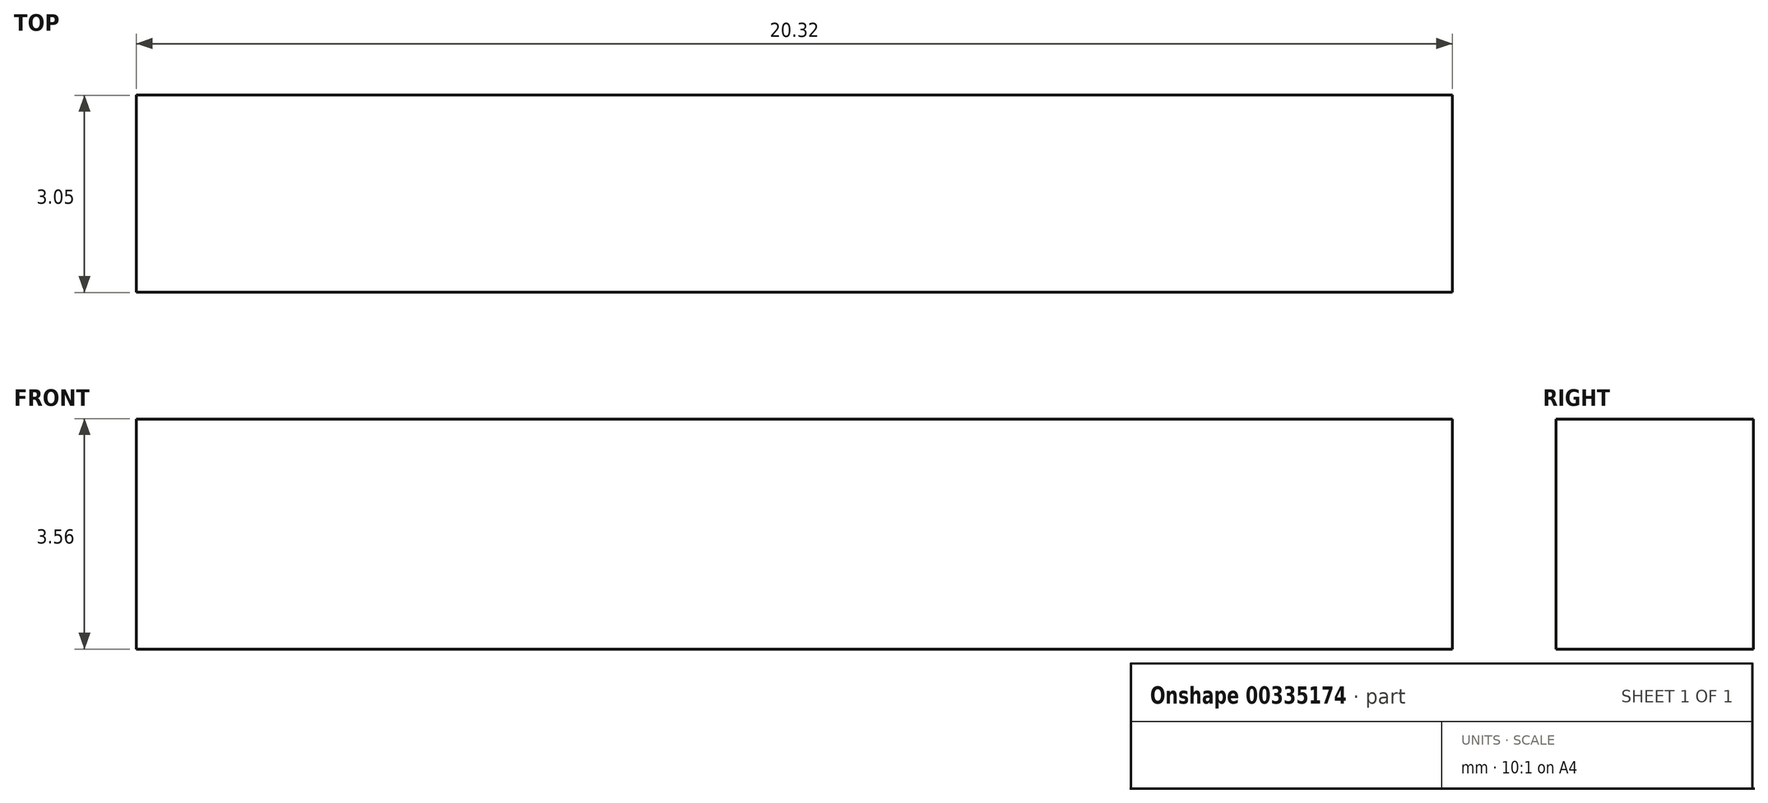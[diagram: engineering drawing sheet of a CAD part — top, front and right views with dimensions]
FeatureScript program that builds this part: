
annotation { "Feature Type Name" : "Feature", "Feature Type Description" : "" }
export const myFeature = defineFeature(function(context is Context, id is Id, definition is map)
    precondition{}
    {
        {
            var Q0;
            Q0=qCreatedBy(makeId("Top.planeOp"),FACE);
            var sketch = newSketch(context, id + "F0", { "sketchPlane" : qUnion([Q0])});
            skLineSegment(sketch, "E0.bottom", {"start": v(-66.95, 32.73) * mm, "end": v(-46.63, 32.73) * mm});
            skLineSegment(sketch, "E0.top", {"start": v(-66.95, 29.68) * mm, "end": v(-46.63, 29.68) * mm});
            skLineSegment(sketch, "E0.left", {"start": v(-66.95, 32.73) * mm, "end": v(-66.95, 29.68) * mm});
            skLineSegment(sketch, "E0.right", {"start": v(-46.63, 32.73) * mm, "end": v(-46.63, 29.68) * mm});
            skSolve(sketch);
        }
        {
            var Q0;
            Q0=makeQuery(id+"F0.imprint","IMPRINT",FACE,{"disambiguationData":[TD([[makeQuery(id+"F0.imprint","IMPRINT",EDGE,{"derivedFrom":sQuery(id+"F0.wireOp",EDGE,"E0.bottom")}),-1.0]])]});
            extrude(context, id + "F1", {"entities" : qUnion([Q0]), "depth" : 3.56 * mm});
        }
    });
